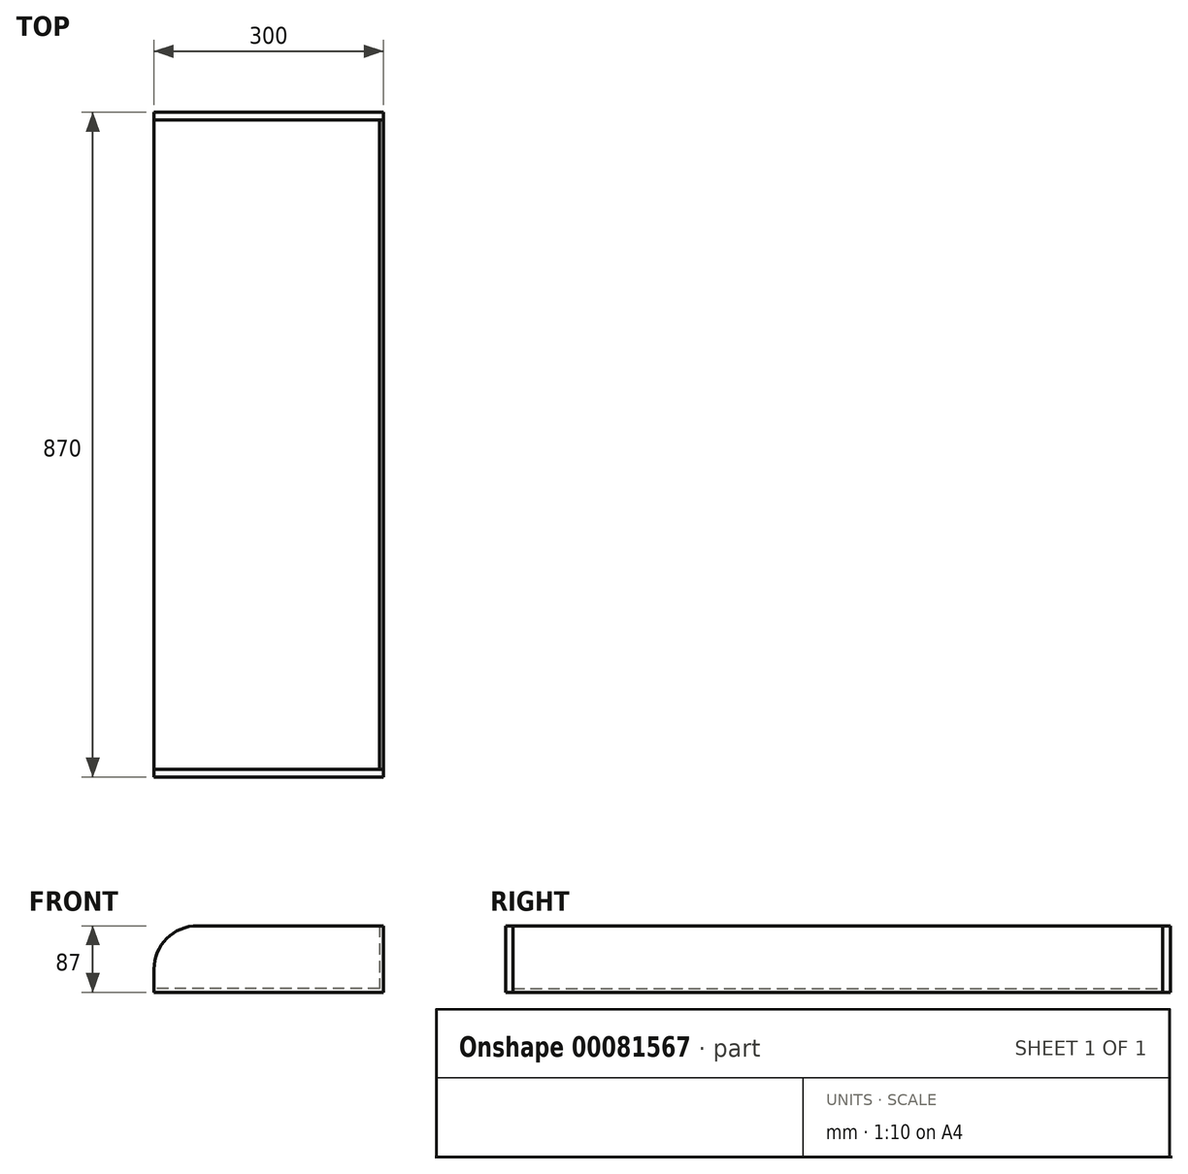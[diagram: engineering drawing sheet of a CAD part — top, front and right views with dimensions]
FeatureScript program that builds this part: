
annotation { "Feature Type Name" : "Feature", "Feature Type Description" : "" }
export const myFeature = defineFeature(function(context is Context, id is Id, definition is map)
    precondition{}
    {
        {
            var Q0;
            Q0=qCreatedBy(makeId("Front.planeOp"),FACE);
            var sketch = newSketch(context, id + "F0", { "sketchPlane" : qUnion([Q0])});
            skArc(sketch, "E0", {"start": v(-243, 57) * mm, "mid": v(-283.3, 40.3) * mm, "end": v(-300, 0) * mm});
            skLineSegment(sketch, "E1", {"start": v(-300, 0) * mm, "end": v(-300, -30) * mm});
            skLineSegment(sketch, "E2", {"start": v(-300, -30) * mm, "end": v(0, -30) * mm});
            skLineSegment(sketch, "E3", {"start": v(0, -30) * mm, "end": v(0, 57) * mm});
            skLineSegment(sketch, "E4", {"start": v(0, 57) * mm, "end": v(-243, 57) * mm});
            skSolve(sketch);
        }
        {
            var Q0;
            Q0 = qSketchRegion(id + "F0", true);
            extrude(context, id + "F1", {"entities" : qUnion([Q0]), "depth" : 10 * mm});
        }
        {
            var Q0;
            Q0=makeQuery(id+"F1.opExtrude","CAP_FACE",FACE,{"disambiguationData":[OSD([sQuery(id+"F0.wireOp",EDGE,"E0"),sQuery(id+"F0.wireOp",EDGE,"E1"),sQuery(id+"F0.wireOp",EDGE,"E2"),sQuery(id+"F0.wireOp",EDGE,"E3"),sQuery(id+"F0.wireOp",EDGE,"E4")])],"isStart":false});
            var sketch = newSketch(context, id + "F2", { "sketchPlane" : qUnion([Q0])});
            skLineSegment(sketch, "E5", {"start": v(-300, -30) * mm, "end": v(0, -30) * mm});
            skLineSegment(sketch, "E6", {"start": v(0, -30) * mm, "end": v(0, 57) * mm});
            skLineSegment(sketch, "E7", {"start": v(0, 57) * mm, "end": v(-5, 57) * mm});
            skLineSegment(sketch, "E8", {"start": v(-5, 57) * mm, "end": v(-5, -25) * mm});
            skLineSegment(sketch, "E9", {"start": v(-5, -25) * mm, "end": v(-300, -25) * mm});
            skLineSegment(sketch, "E10", {"start": v(-300, -25) * mm, "end": v(-300, -30) * mm});
            skSolve(sketch);
        }
        {
            var Q0;
            Q0 = qSketchRegion(id + "F2", true);
            extrude(context, id + "F3", {"entities" : qUnion([Q0]), "depth" : 850 * mm});
        }
        {
            var Q0;
            Q0=makeQuery(id+"F1.opExtrude","SWEPT_BODY",BODY,{"disambiguationData":[OSD([sQuery(id+"F0.wireOp",EDGE,"E0"),sQuery(id+"F0.wireOp",EDGE,"E1"),sQuery(id+"F0.wireOp",EDGE,"E2"),sQuery(id+"F0.wireOp",EDGE,"E3"),sQuery(id+"F0.wireOp",EDGE,"E4")])]});
            transform(context, id + "F4", {"entities" : qUnion([Q0]), "transformType" : TransformType.TRANSLATION_3D, "dx" : 0 * mm, "dy" : -860 * mm, "dz" : 0 * mm, "makeCopy" : true});
        }
    });
